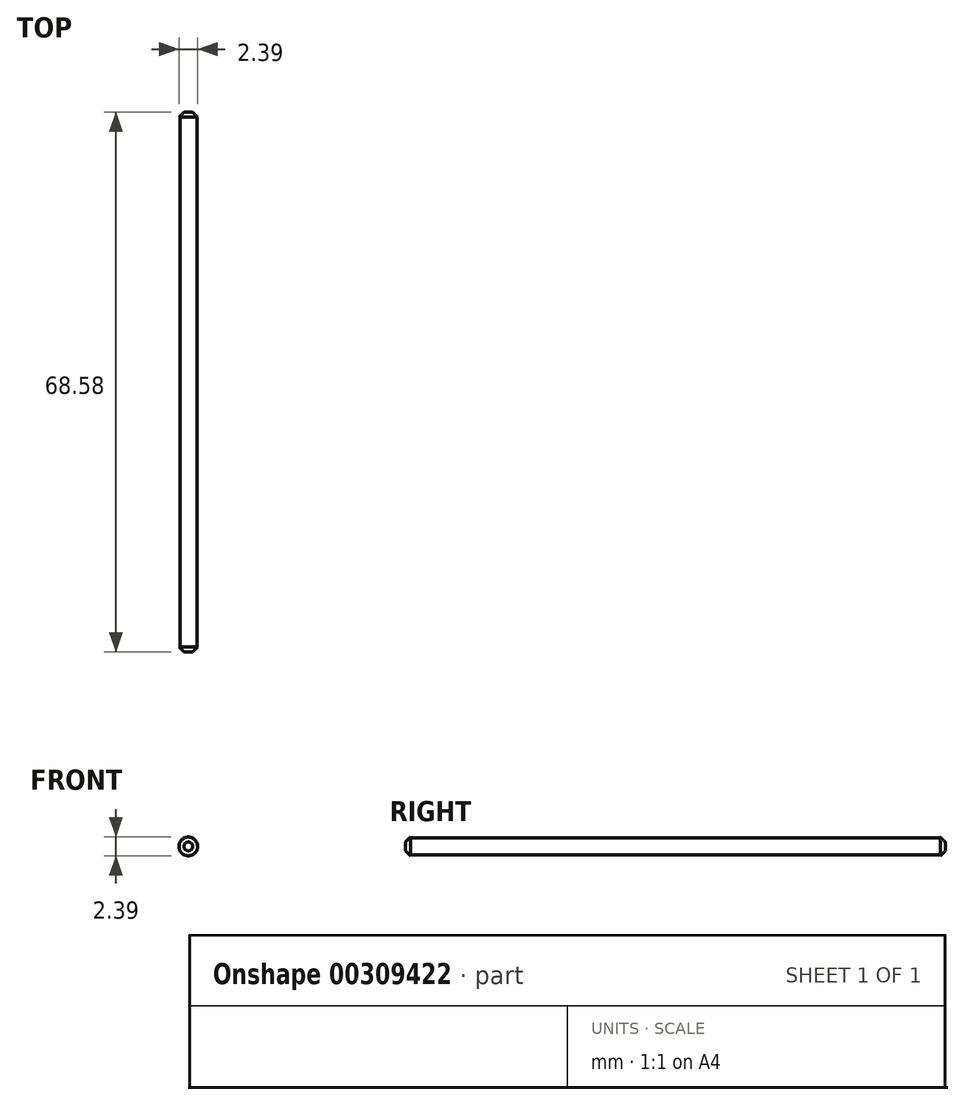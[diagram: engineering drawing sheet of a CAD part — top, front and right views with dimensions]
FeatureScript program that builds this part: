
annotation { "Feature Type Name" : "Feature", "Feature Type Description" : "" }
export const myFeature = defineFeature(function(context is Context, id is Id, definition is map)
    precondition{}
    {
        {
            var Q0;
            Q0=qCreatedBy(makeId("Front.planeOp"),FACE);
            var sketch = newSketch(context, id + "F0", { "sketchPlane" : qUnion([Q0])});
            skCircle(sketch, "E0", {"center": v(9.3, 10.93) * mm, "radius": 1.08 * mm});
            skSolve(sketch);
        }
        {
            var Q0;
            Q0=makeQuery(id+"F0.imprint","IMPRINT",FACE,{"disambiguationData":[TD([[makeQuery(id+"F0.imprint","IMPRINT",EDGE,{"derivedFrom":sQuery(id+"F0.wireOp",EDGE,"E0")}),1.0]])]});
            extrude(context, id + "F1", {"entities" : qUnion([Q0]), "depth" : 66.8 * mm});
        }
        {
            var Q0;
            Q0=makeQuery(id+"F1.opExtrude","CAP_FACE",FACE,{"disambiguationData":[OSD([sQuery(id+"F0.wireOp",EDGE,"E0")])],"isStart":true});
            var sketch = newSketch(context, id + "F2", { "sketchPlane" : qUnion([Q0])});
            skCircle(sketch, "E1", {"center": v(-9.3, 10.93) * mm, "radius": 1.15 * mm});
            skSolve(sketch);
        }
        {
            var Q0;
            Q0=makeQuery(id+"F2.imprint","IMPRINT",FACE,{"disambiguationData":[TD([[makeQuery(id+"F2.imprint","IMPRINT",EDGE,{"derivedFrom":makeQuery(id+"F1.opExtrude","CAP_EDGE",EDGE,{"disambiguationData":[OSD([sQuery(id+"F0.wireOp",EDGE,"E0")])],"isStart":true})}),-1.0]])]});
            extrude(context, id + "F3", {"entities" : qUnion([Q0]), "operationType" : NewBodyOperationType.ADD, "depth" : 0.5 * mm});
        }
        {
            var Q0;
            Q0=makeQuery(id+"F1.opExtrude","CAP_FACE",FACE,{"disambiguationData":[OSD([sQuery(id+"F0.wireOp",EDGE,"E0")])],"isStart":false});
            var sketch = newSketch(context, id + "F4", { "sketchPlane" : qUnion([Q0])});
            skCircle(sketch, "E2", {"center": v(9.3, 10.93) * mm, "radius": 1.24 * mm});
            skSolve(sketch);
        }
        {
            var Q0;
            Q0=makeQuery(id+"F4.imprint","IMPRINT",FACE,{"disambiguationData":[TD([[makeQuery(id+"F4.imprint","IMPRINT",EDGE,{"derivedFrom":sQuery(id+"F4.wireOp",EDGE,"E2")}),1.0]])]});
            var Q1;
            Q1=makeQuery(id+"F4.imprint","IMPRINT",FACE,{"disambiguationData":[TD([[makeQuery(id+"F4.imprint","IMPRINT",EDGE,{"derivedFrom":makeQuery(id+"F1.opExtrude","CAP_EDGE",EDGE,{"disambiguationData":[OSD([sQuery(id+"F0.wireOp",EDGE,"E0")])],"isStart":false})}),1.0]])]});
            extrude(context, id + "F5", {"entities" : qUnion([Q0, Q1]), "operationType" : NewBodyOperationType.ADD, "depth" : 0.64 * mm});
        }
        {
            var Q0;
            Q0=makeQuery(id+"F3.opExtrude","CAP_FACE",FACE,{"disambiguationData":[OSD([sQuery(id+"F0.wireOp",EDGE,"E0")])],"isStart":false});
            var sketch = newSketch(context, id + "F6", { "sketchPlane" : qUnion([Q0])});
            skCircle(sketch, "E3", {"center": v(-9.3, 10.93) * mm, "radius": 1.24 * mm});
            skSolve(sketch);
        }
        {
            var Q0;
            Q0=makeQuery(id+"F6.imprint","IMPRINT",FACE,{"disambiguationData":[TD([[makeQuery(id+"F6.imprint","IMPRINT",EDGE,{"derivedFrom":sQuery(id+"F6.wireOp",EDGE,"E3")}),1.0]])]});
            var Q1;
            Q1=makeQuery(id+"F6.imprint","IMPRINT",FACE,{"disambiguationData":[TD([[makeQuery(id+"F6.imprint","IMPRINT",EDGE,{"derivedFrom":makeQuery(id+"F3.opExtrude","CAP_EDGE",EDGE,{"disambiguationData":[OSD([sQuery(id+"F0.wireOp",EDGE,"E0")])],"isStart":false})}),-1.0]])]});
            extrude(context, id + "F7", {"entities" : qUnion([Q0, Q1]), "operationType" : NewBodyOperationType.ADD, "depth" : 0.64 * mm});
        }
        {
            var Q0;
            Q0=makeQuery(id+"F7.opExtrude","CAP_EDGE",EDGE,{"disambiguationData":[OSD([sQuery(id+"F6.wireOp",EDGE,"E3")])],"isStart":false});
            chamfer(context, id + "F8", {"entities" : qUnion([Q0]), "width" : 0.69 * mm, "tangentPropagation" : true});
        }
        {
            var Q0;
            Q0=makeQuery(id+"F5.opExtrude","CAP_EDGE",EDGE,{"disambiguationData":[OSD([sQuery(id+"F4.wireOp",EDGE,"E2")])],"isStart":false});
            chamfer(context, id + "F9", {"entities" : qUnion([Q0]), "width" : 0.69 * mm, "tangentPropagation" : true});
        }
    });
